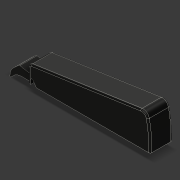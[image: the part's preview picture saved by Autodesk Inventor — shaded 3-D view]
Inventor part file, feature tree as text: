
AUTODESK INVENTOR PART (.ipt)
format: ipt  version: 2020.2 (Build 242310000, 310)  size: 188,416 bytes
history: native  units: mm
features: extrude x3, fillet x3, other x1
ambient origin geometry x8: Origin, YZ Plane, XZ Plane, XY Plane, X Axis, Y Axis, Z Axis, Center Point
bodies: Solid1 (feature_tree)
feature tree (7):
  other  "Profile Sketch"
  extrude  "Main Key"  Depth=0.6mm
  extrude  "Extrusion2"  TaperAngle=45.0deg  [1 undecoded]
  fillet  "Fillet1"  Radius=55.0mm
  extrude  "Extrusion3"  Depth=10.275mm TaperAngle=0.0deg
  fillet  "Fillet2"  Radius=9.572811mm
  fillet  "Fillet3"  Radius=2.5mm
note: 1 required parameter value undecoded (feature->parameter linkage not recoverable at this tier; creation-order binding heuristic only, values carry confidence <= 0.55)
